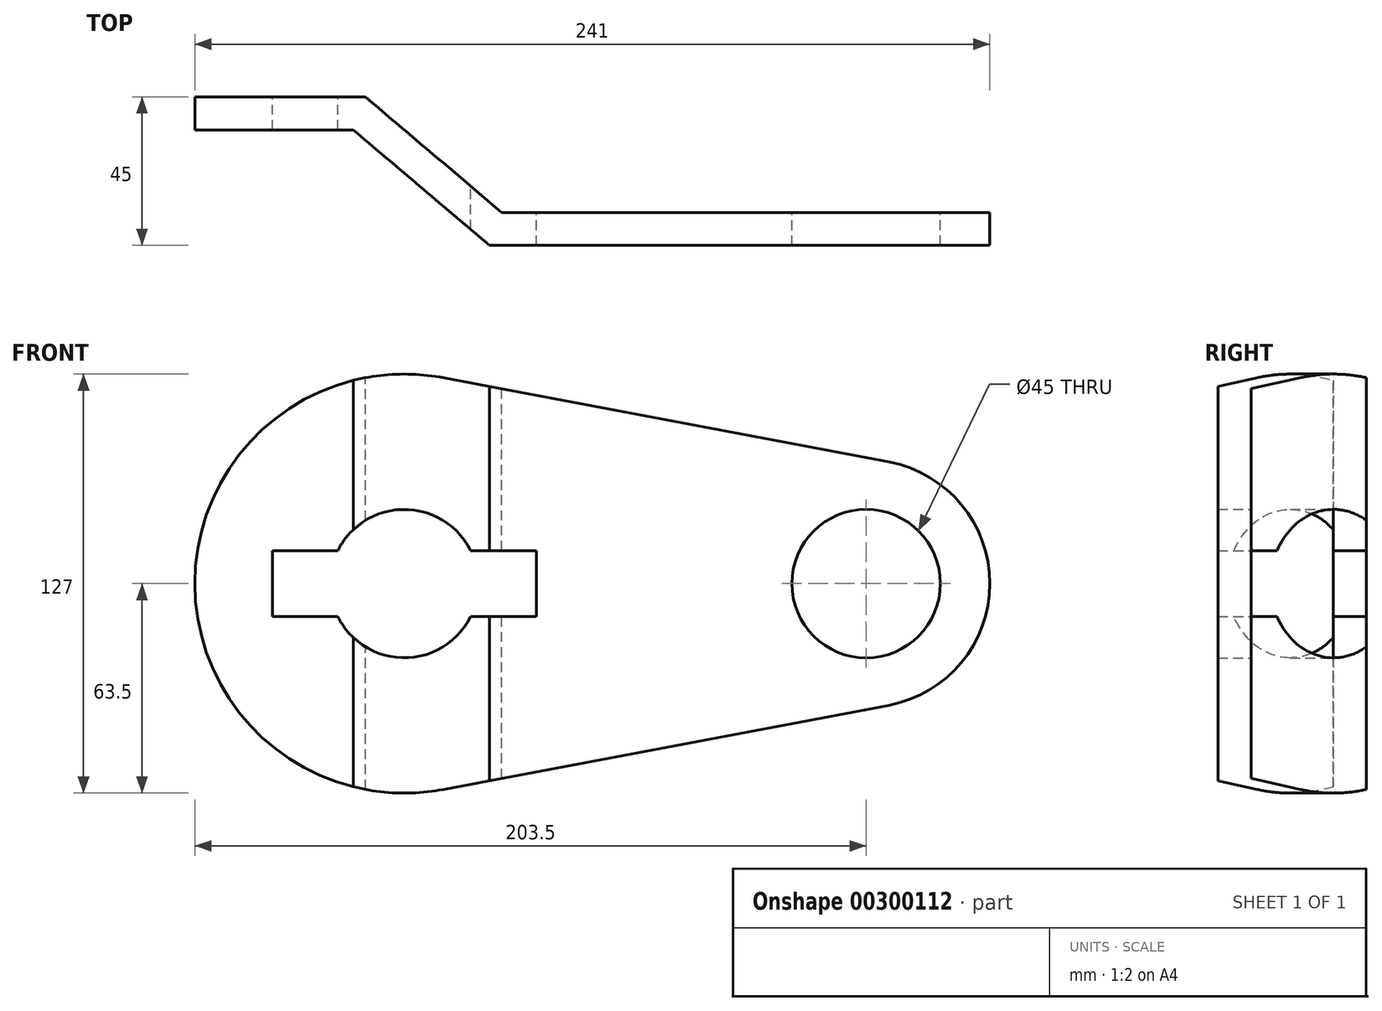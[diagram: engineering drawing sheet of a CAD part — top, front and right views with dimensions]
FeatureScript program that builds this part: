
annotation { "Feature Type Name" : "Feature", "Feature Type Description" : "" }
export const myFeature = defineFeature(function(context is Context, id is Id, definition is map)
    precondition{}
    {
        {
            var Q0;
            Q0=qCreatedBy(makeId("Front.planeOp"),FACE);
            var sketch = newSketch(context, id + "F0", { "sketchPlane" : qUnion([Q0])});
            skCircle(sketch, "E0", {"center": v(-63.5, 0) * mm, "radius": 63.5 * mm});
            skCircle(sketch, "E1", {"center": v(76.5, 0) * mm, "radius": 37.5 * mm});
            skLineSegment(sketch, "E2", {"start": v(-51.7, 62.4) * mm, "end": v(83.46, 36.85) * mm});
            skLineSegment(sketch, "E3", {"start": v(-51.7, -62.4) * mm, "end": v(83.46, -36.85) * mm});
            skCircle(sketch, "E4", {"center": v(76.5, 0) * mm, "radius": 22.5 * mm});
            skCircle(sketch, "E5", {"center": v(-63.5, 0) * mm, "radius": 22.5 * mm});
            skLineSegment(sketch, "E6.bottom", {"start": v(-23.5, -10) * mm, "end": v(-103.5, -10) * mm});
            skLineSegment(sketch, "E6.top", {"start": v(-23.5, 10) * mm, "end": v(-103.5, 10) * mm});
            skLineSegment(sketch, "E6.left", {"start": v(-23.5, -10) * mm, "end": v(-23.5, 10) * mm});
            skLineSegment(sketch, "E6.right", {"start": v(-103.5, -10) * mm, "end": v(-103.5, 10) * mm});
            skSolve(sketch);
        }
        {
            var Q0;
            {var subQ11=sQuery(id+"F0.wireOp",EDGE,"E6.left");Q0=makeQuery(id+"F0.imprint","IMPRINT",FACE,{"disambiguationData":[TD([[makeQuery(id+"F0.imprint","IMPRINT",EDGE,{"derivedFrom":subQ11}),-1.0]])]});}
            var Q1;
            {var subQ0=sQuery(id+"F0.wireOp",EDGE,"E2");Q1=makeQuery(id+"F0.imprint","IMPRINT",FACE,{"disambiguationData":[TD([[makeQuery(id+"F0.imprint","IMPRINT",EDGE,{"derivedFrom":subQ0}),-1.0]])]});}
            var Q2;
            Q2=makeQuery(id+"F0.imprint","IMPRINT",FACE,{"disambiguationData":[TD([[makeQuery(id+"F0.imprint","IMPRINT",EDGE,{"derivedFrom":sQuery(id+"F0.wireOp",EDGE,"E4")}),-1.0]])]});
            extrude(context, id + "F1", {"entities" : qUnion([Q0, Q1, Q2]), "depth" : 25 * mm});
        }
        {
            var Q0;
            {var subQ11=sQuery(id+"F0.wireOp",EDGE,"E6.left");Q0=makeQuery(id+"F0.imprint","IMPRINT",FACE,{"disambiguationData":[TD([[makeQuery(id+"F0.imprint","IMPRINT",EDGE,{"derivedFrom":subQ11}),-1.0]])]});}
            extrude(context, id + "F2", {"entities" : qUnion([Q0]), "operationType" : NewBodyOperationType.ADD, "oppositeDirection" : true, "depth" : 20 * mm});
        }
        {
            var Q0;
            Q0=qCreatedBy(makeId("Top.planeOp"),FACE);
            var sketch = newSketch(context, id + "F3", { "sketchPlane" : qUnion([Q0])});
            skLineSegment(sketch, "E7", {"start": v(-158.53, 20) * mm, "end": v(-75.33, 20) * mm});
            skLineSegment(sketch, "E8", {"start": v(-75.33, 20) * mm, "end": v(-34, -15) * mm});
            skLineSegment(sketch, "E9", {"start": v(-34, -15) * mm, "end": v(141.55, -15) * mm});
            skLineSegment(sketch, "E10.0", {"start": v(-37.66, -25) * mm, "end": v(141.55, -25) * mm});
            skLineSegment(sketch, "E10.1", {"start": v(-79, 10) * mm, "end": v(-37.66, -25) * mm});
            skLineSegment(sketch, "E10.2", {"start": v(-158.53, 10) * mm, "end": v(-79, 10) * mm});
            skLineSegment(sketch, "E11", {"start": v(141.55, -15) * mm, "end": v(141.55, -25) * mm});
            skLineSegment(sketch, "E12", {"start": v(-158.53, 20) * mm, "end": v(-158.53, 10) * mm});
            skSolve(sketch);
        }
        {
            var Q0;
            Q0 = qSketchRegion(id + "F3", true);
            extrude(context, id + "F4", {"entities" : qUnion([Q0]), "operationType" : NewBodyOperationType.INTERSECT, "endBound" : BoundingType.THROUGH_ALL, "oppositeDirection" : true, "depth" : 25 * mm, "hasSecondDirection" : true, "secondDirectionBound" : BoundingType.THROUGH_ALL, "secondDirectionOppositeDirection" : false, "secondDirectionDepth" : 25 * mm});
        }
    });
